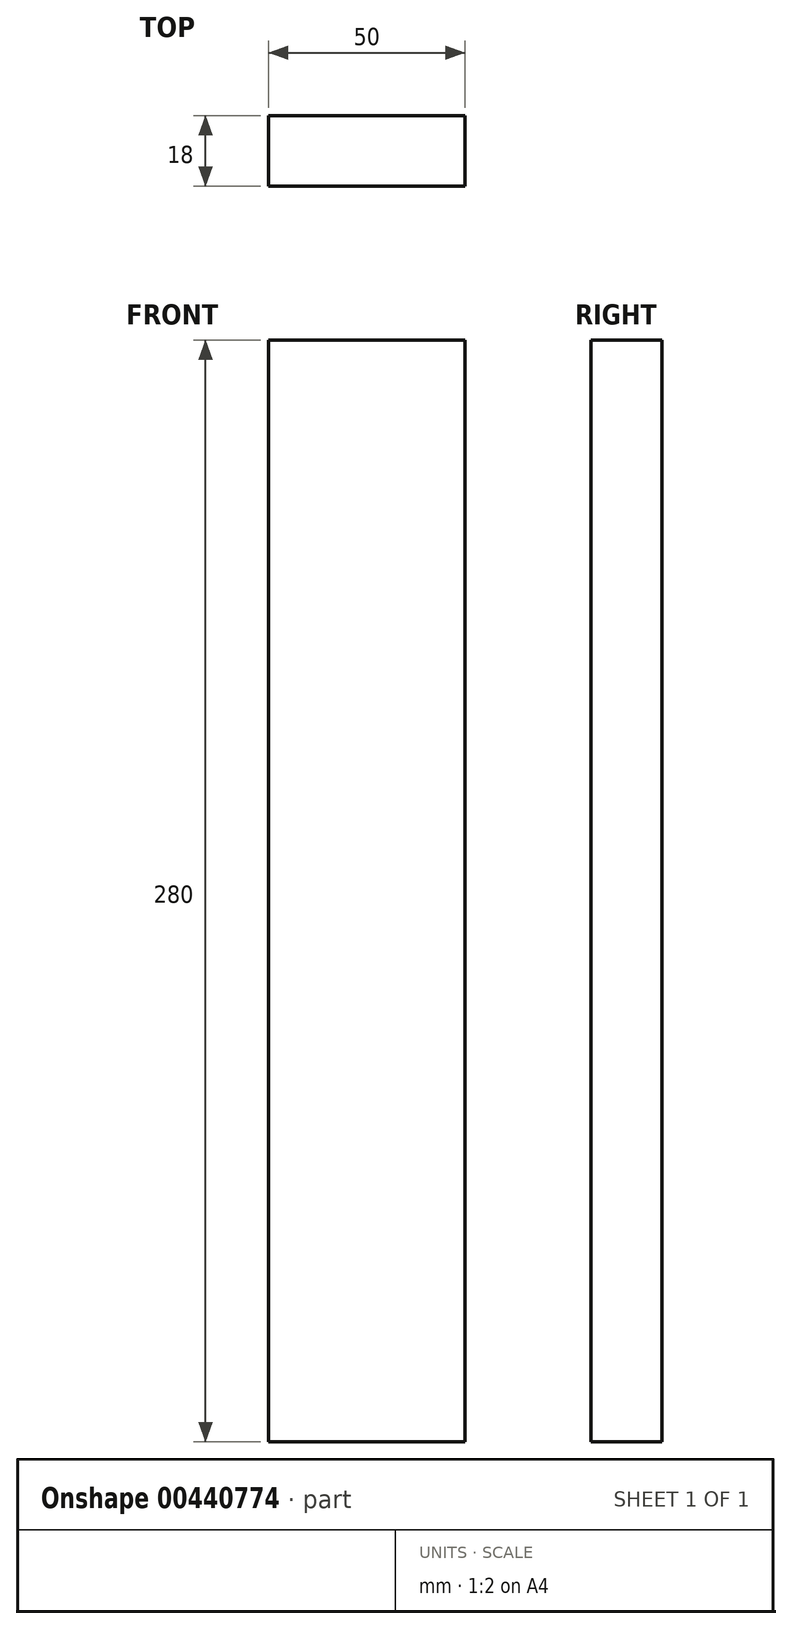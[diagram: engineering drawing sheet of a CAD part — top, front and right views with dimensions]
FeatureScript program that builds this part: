
annotation { "Feature Type Name" : "Feature", "Feature Type Description" : "" }
export const myFeature = defineFeature(function(context is Context, id is Id, definition is map)
    precondition{}
    {
        {
            var Q0;
            Q0=qCreatedBy(makeId("Front.planeOp"),FACE);
            var sketch = newSketch(context, id + "F0", { "sketchPlane" : qUnion([Q0])});
            skLineSegment(sketch, "E0.bottom", {"start": v(0, 0) * mm, "end": v(-50, 0) * mm});
            skLineSegment(sketch, "E0.top", {"start": v(0, 280) * mm, "end": v(-50, 280) * mm});
            skLineSegment(sketch, "E0.left", {"start": v(0, 0) * mm, "end": v(0, 280) * mm});
            skLineSegment(sketch, "E0.right", {"start": v(-50, 0) * mm, "end": v(-50, 280) * mm});
            skSolve(sketch);
        }
        {
            var Q0;
            Q0 = qSketchRegion(id + "F0", true);
            extrude(context, id + "F1", {"entities" : qUnion([Q0]), "depth" : 18 * mm});
        }
    });
